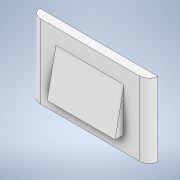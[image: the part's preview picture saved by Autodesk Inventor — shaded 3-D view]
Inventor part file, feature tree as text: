
AUTODESK INVENTOR PART (.ipt)
format: ipt  version: 2022 (Build 260153000, 153)  size: 130,048 bytes
history: native  units: mm
features: sketch x3, other x2, extrude x2, fillet x2
ambient origin geometry x8: Origin, YZ Plane, XZ Plane, XY Plane, X Axis, Y Axis, Z Axis, Center Point
bodies: Body1 (feature_tree)
feature tree (9):
  other  "솔리드1"
  extrude  "돌출1"  Depth=120.0mm
  sketch  "스케치2"
  other  "작업 평면1"
  extrude  "돌출2"  Depth=75.0mm
  fillet  "모깎기1"  Radius=9.0mm
  fillet  "모깎기2"  Radius=44.0mm
  sketch  "스케치1"
  sketch  "스케치3"
